# Revit family: 231310004017970
name_source: partatom
category: Perfiles
revit_build: Autodesk Revit 2018 (Build: 20190510_1515(x64)
units: mm (PartAtom-declared; Revit-internal decimal feet)

## family parameters
Forma de sección = Sin definir
Rotar con componente = Sí
Uso de perfil = Barrido de muro

## types (1)
- VERSETTA STONE TRIM STONE 20CM TAUPE TIRA 0.9MT
    Altura = 100 mm  [stored 0.328084 ft]
    Aplicacion = Accesorio para la instalación de Versetta Stone
    Color = TAUPE
    Dimension = 200 mm  [stored 0.656168 ft]
    Empresa = CNP SPA.
    Espesor = 50 mm  [stored 0.164042 ft]
    Largo = 900 mm  [stored 2.95276 ft]
    Material = <Por categoría>
    Modelo = VERSETTA STONE TRIM STONE 20CM TAUPE
    Nombre SKU = VERSETTA STONE TRIM STONE 20CM TAUPE TIRA 0.9MT
    Num SKUs = 231310004017970
    URL = https://www.empresascnp.cl
    Unidad = Tiras de 0.9 Metros
    Url Ficha tecnica = https://empresascnp.cl

note: [stored X ft] marks values corroborated as IEEE doubles in the binary element streams (Revit-internal decimal feet)

## geometry (parser evidence)
native form markers: Blend x4
no freeform markers — native parametric forms only
